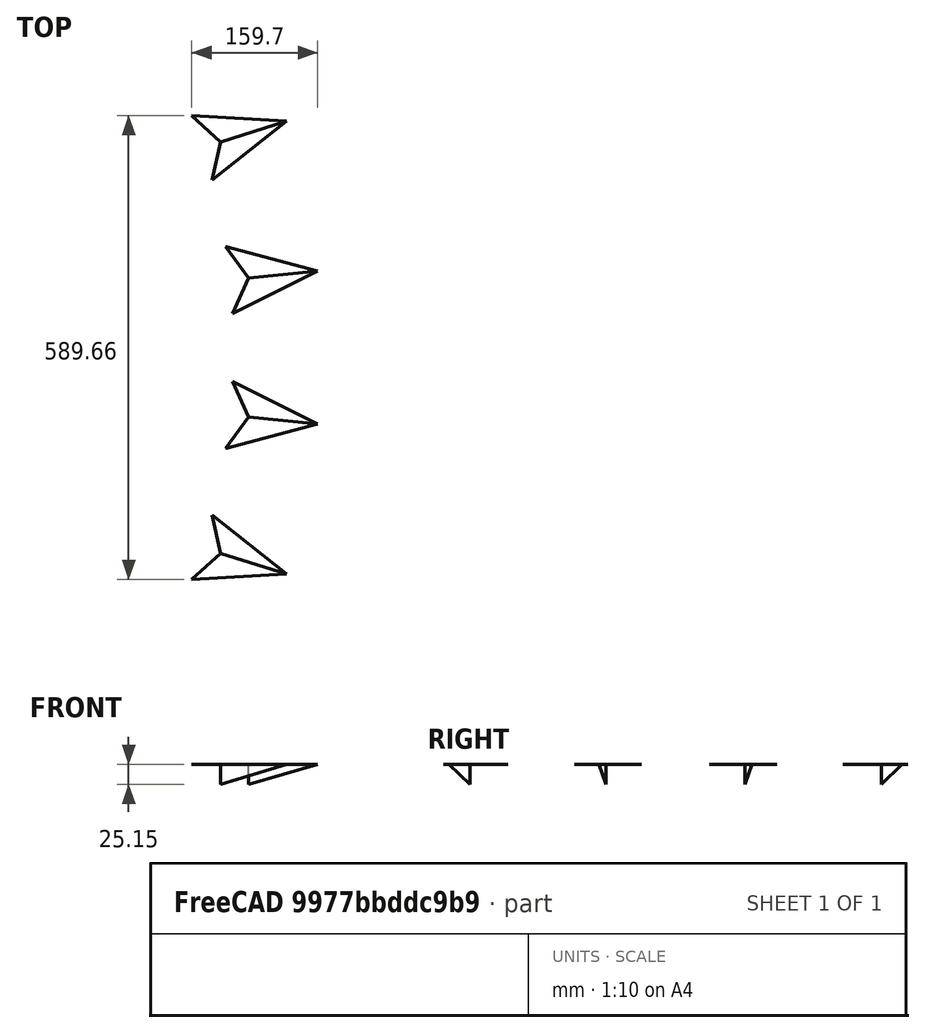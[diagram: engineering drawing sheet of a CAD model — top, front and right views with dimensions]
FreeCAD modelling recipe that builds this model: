
FCSTD DOCUMENT  (FreeCAD 1.1R38827 (Git))
Label: composit_stand3_sink_hand_main
License: All rights reserved
LicenseURL: http://en.wikipedia.org/wiki/All_rights_reserved
objects: Part::FeaturePython×3, PartDesign::SubShapeBinder×1, Sketcher::SketchObject×1, Part::Feature×1
note: 7 computed .brp shape members not serialized (recipe doc carries the construction recipe); baked Part::Feature solids carry a one-line shape summary decoded from their .brp
EXTERNAL_REF file=composit_stand3_sink_main.FCStd obj=Sketch002

FEATURE [PartDesign::SubShapeBinder] Binder
  BindCopyOnChange = 0
  BindMode = 0
  ClaimChildren = true
  Fuse = false
  MakeFace = true
  OffsetFill = false
  OffsetIntersection = false
  OffsetJoinType = 0
  OffsetOpenResult = false
  PartialLoad = false
  Relative = false
  Support = -> [<external composit_stand3_sink_main.FCStd>#Sketch002]
  _Version = 2
FEATURE [Sketcher::SketchObject] Sketch
  ArcFitTolerance = 0
  ExternalGeometry = -> [Binder]
  FullyConstrained = false
  MakeInternals = false
  sketch-geometry (1):
    g0: LineSegment [constr] StartX=127.38 StartY=229.314 StartZ=0 EndX=191.98 EndY=273.234 EndZ=0
  constraints (1):
    c: PointOnObject(g-4,g0)
FEATURE [Part::FeaturePython] PolarArray  # WARN: FeaturePython — macro-defined, semantics opaque (R4)
  Alignment = 0
  AttacherType = Attacher::AttachEngine3D
  AttachmentSupport = -> [Sketch]
  CellStart = A1
  Count = 2
  DistributionLaw = 0
  EndInclusive = true
  ExposePlacement = false
  FlipX = false
  FlipZ = false
  GeneratorMode = 0
  MarkerShape = 1
  MarkerSize = 100
  NumElements = 2
  OrientMode = 2
  Placement = pos=(-639.136,0,0) rot=(0,0,1;0rad)
  Radius = 872.481
  Reverse = false
  SpanEnd = 17.4264
  SpanStart = 5.8088
  Step = 11.6176
  Type = lattice2PolarArray2.PolarArray
  UseArcRadius = false
  UseArcRange = 0
  VSGVersion = 1
  Values = 5.808800000000001 | 17.4264
  ValuesSource = 2
  isLattice = 1
  expr: SpanStart = SpanEnd / 3
FEATURE [Part::FeaturePython] Mirror  label="Mirror of PolarArray"  # WARN: FeaturePython — macro-defined, semantics opaque (R4)
  ExposePlacement = false
  FlipX = false
  FlipY = true
  FlipZ = false
  MarkerShape = 1
  MarkerSize = 0
  NumElements = 2
  Object = -> PolarArray
  ObjectTraversal = 0
  Type = lattice2Mirror.LatticeMirror
  isLattice = 1
FEATURE [Part::FeaturePython] Join  label="sink_hand_holes"  # WARN: FeaturePython — macro-defined, semantics opaque (R4)
  ExposePlacement = false
  Interleave = false
  Links = -> [PolarArray,Mirror]
  MarkerShape = 1
  MarkerSize = 0
  NumElements = 4
  Type = lattice2JoinArrays.JoinArrays
  isLattice = 1
FEATURE [Part::Feature] Sketch002
  shape: bbox 70.89 x 293 x 2e-07 mm, 0 faces, 0 solids (baked)
